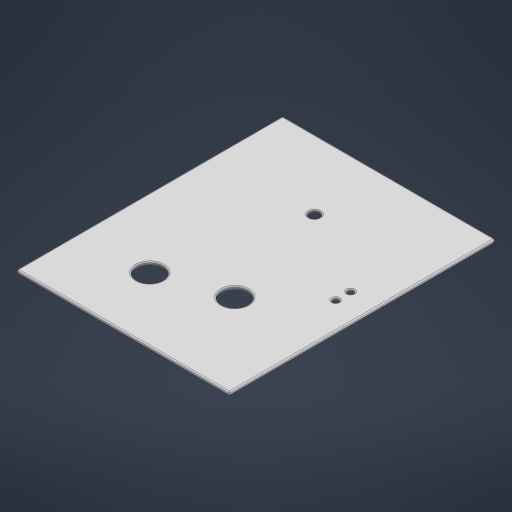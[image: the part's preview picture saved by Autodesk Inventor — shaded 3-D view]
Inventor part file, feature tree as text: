
AUTODESK INVENTOR PART (.ipt)
format: ipt  version: 2023 (Build 270158000, 158)  size: 264,704 bytes
history: native  units: mm
features: extrude x1, fillet x1, other x1
ambient origin geometry x8: Origin, YZ Plane, XZ Plane, XY Plane, X Axis, Y Axis, Z Axis, Center Point
bodies: Solid1 (feature_tree)
feature tree (3):
  extrude  "and"  Depth=200.0mm
  fillet  "Fillet1"  Radius=250.0mm
  other  "page_lines"
